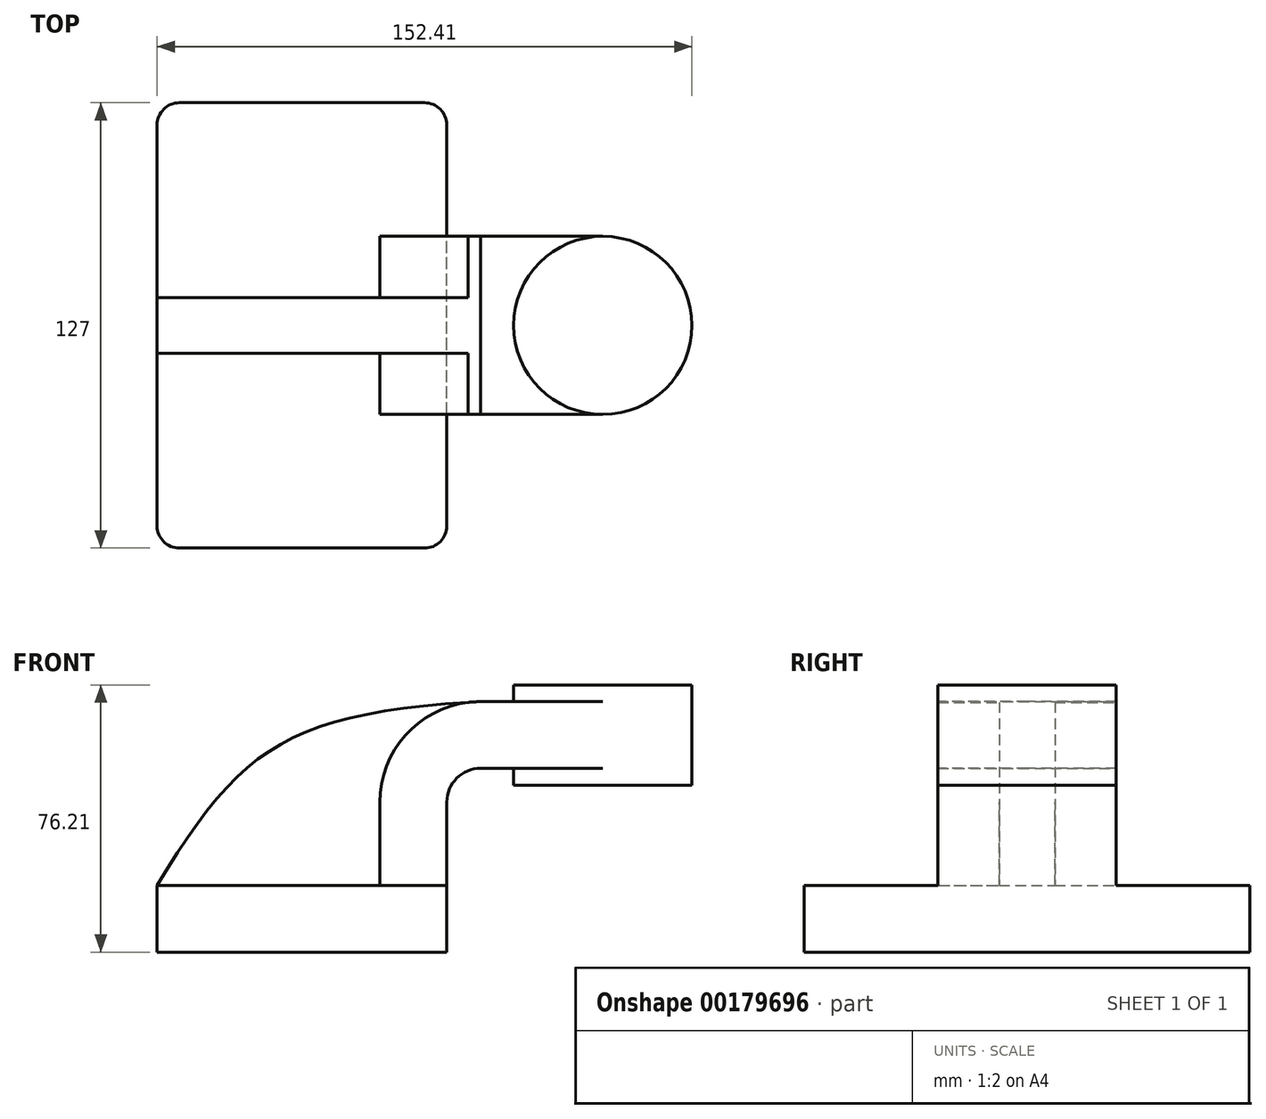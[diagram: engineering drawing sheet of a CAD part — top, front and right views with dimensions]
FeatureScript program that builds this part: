
annotation { "Feature Type Name" : "Feature", "Feature Type Description" : "" }
export const myFeature = defineFeature(function(context is Context, id is Id, definition is map)
    precondition{}
    {
        {
            var Q0;
            Q0=qCreatedBy(makeId("Front.planeOp"),FACE);
            var sketch = newSketch(context, id + "F0", { "sketchPlane" : qUnion([Q0])});
            skLineSegment(sketch, "E0.bottom", {"start": v(41.27, 9.53) * mm, "end": v(-41.28, 9.53) * mm});
            skLineSegment(sketch, "E0.top", {"start": v(41.28, -9.52) * mm, "end": v(-41.27, -9.52) * mm});
            skLineSegment(sketch, "E0.left", {"start": v(41.28, 9.53) * mm, "end": v(41.28, -9.52) * mm});
            skLineSegment(sketch, "E0.right", {"start": v(-41.28, 9.53) * mm, "end": v(-41.27, -9.52) * mm});
            skPoint(sketch, "E0.middle", {"position": v(0, 0) * mm});
            skLineSegment(sketch, "E1.bottom", {"start": v(111.12, 38.1) * mm, "end": v(60.32, 38.1) * mm});
            skLineSegment(sketch, "E1.top", {"start": v(111.12, 66.68) * mm, "end": v(60.32, 66.68) * mm});
            skLineSegment(sketch, "E1.left", {"start": v(111.12, 38.1) * mm, "end": v(111.12, 66.68) * mm});
            skLineSegment(sketch, "E1.right", {"start": v(60.32, 38.1) * mm, "end": v(60.32, 66.68) * mm});
            skPoint(sketch, "E1.middle", {"position": v(85.72, 52.39) * mm});
            skLineSegment(sketch, "E2", {"start": v(41.28, 9.53) * mm, "end": v(41.28, 33.25) * mm});
            skPoint(sketch, "E3.endSnap0", {"position": v(60.32, 52.39) * mm});
            skArc(sketch, "E4", {"start": v(41.27, 33.25) * mm, "mid": v(44.1, 40.06) * mm, "end": v(50.9, 42.88) * mm});
            skLineSegment(sketch, "E5", {"start": v(50.9, 42.88) * mm, "end": v(85.72, 42.88) * mm});
            skFitSpline(sketch, "E6", {"points": [v(50.9, 61.93) * mm, v(-41.28, 9.53) * mm], "startDerivative": vector(-164.5, -9.49) * mm, "endDerivative": vector(-71.06, -117.92) * mm});
            skLineSegment(sketch, "E7.0", {"start": v(50.9, 61.93) * mm, "end": v(85.72, 61.93) * mm});
            skArc(sketch, "E7.1", {"start": v(22.23, 33.25) * mm, "mid": v(30.62, 53.53) * mm, "end": v(50.9, 61.93) * mm});
            skLineSegment(sketch, "E7.2", {"start": v(22.23, 9.53) * mm, "end": v(22.23, 33.25) * mm});
            skLineSegment(sketch, "E8", {"start": v(85.72, 38.1) * mm, "end": v(85.72, 66.68) * mm});
            skSolve(sketch);
        }
        {
            var Q0;
            Q0=makeQuery(id+"F0.imprint","IMPRINT",FACE,{"disambiguationData":[TD([[makeQuery(id+"F0.imprint","IMPRINT",EDGE,{"derivedFrom":sQuery(id+"F0.wireOp",EDGE,"E0.top")}),-1.0]])]});
            extrude(context, id + "F1", {"entities" : qUnion([Q0]), "endBound" : BoundingType.SYMMETRIC, "depth" : 127 * mm});
        }
        {
            var Q0;
            {var subQ5=sQuery(id+"F0.wireOp",EDGE,"ryHTmhne-aWk1-Qow2-LsZY-GAX3mDUKrZVP");Q0=makeQuery(id+"F0.imprint","IMPRINT",FACE,{"disambiguationData":[TD([[makeQuery(id+"F0.imprint","IMPRINT",EDGE,{"derivedFrom":subQ5}),1.0]])]});}
            var Q1;
            {var subQ1=sQuery(id+"F0.wireOp",EDGE,"E2");Q1=makeQuery(id+"F0.imprint","IMPRINT",FACE,{"disambiguationData":[TD([[makeQuery(id+"F0.imprint","IMPRINT",EDGE,{"derivedFrom":subQ1}),1.0]])]});}
            var Q2;
            {var subQ0=sQuery(id+"F0.wireOp",EDGE,"E5");var subQ1=sQuery(id+"F0.wireOp",EDGE,"E1.right");var subQ2=makeQuery(id+"F0.imprint","INTERSECT",VERTEX,{"derivedFrom":[subQ1,subQ0]});Q2=makeQuery(id+"F0.imprint","IMPRINT",FACE,{"disambiguationData":[TD([[makeQuery(id+"F0.imprint","IMPRINT",EDGE,{"disambiguationData":[TD([[subQ2,-1.0]])],"derivedFrom":subQ1}),-1.0]])]});}
            extrude(context, id + "F2", {"entities" : qUnion([Q0, Q1, Q2]), "operationType" : NewBodyOperationType.ADD, "endBound" : BoundingType.SYMMETRIC, "depth" : 50.8 * mm});
        }
        {
            var Q0;
            {var subQ3=sQuery(id+"F0.wireOp",EDGE,"E7.2");Q0=makeQuery(id+"F0.imprint","IMPRINT",FACE,{"disambiguationData":[TD([[makeQuery(id+"F0.imprint","IMPRINT",EDGE,{"derivedFrom":subQ3}),1.0]])]});}
            extrude(context, id + "F3", {"entities" : qUnion([Q0]), "operationType" : NewBodyOperationType.ADD, "endBound" : BoundingType.SYMMETRIC, "depth" : 15.88 * mm});
        }
        {
            var Q0;
            {var subQ4=sQuery(id+"F0.wireOp",EDGE,"E1.left");Q0=makeQuery(id+"F0.imprint","IMPRINT",FACE,{"disambiguationData":[TD([[makeQuery(id+"F0.imprint","IMPRINT",EDGE,{"derivedFrom":subQ4}),1.0]])]});}
            var Q1;
            Q1=sQuery(id+"F0.wireOp",EDGE,"E8");
            revolve(context, id + "F4", {"operationType" : NewBodyOperationType.ADD, "entities" : qUnion([Q0]), "axis" : qUnion([Q1]), "revolveType" : RevolveType.FULL});
        }
        {
            var Q0;
            Q0=makeQuery(id+"F1.opExtrude","CAP_EDGE",EDGE,{"disambiguationData":[OSD([sQuery(id+"F0.wireOp",EDGE,"E0.left")])],"isStart":false});
            var Q1;
            Q1=makeQuery(id+"F1.opExtrude","CAP_EDGE",EDGE,{"disambiguationData":[OSD([sQuery(id+"F0.wireOp",EDGE,"E0.right")])],"isStart":false});
            var Q2;
            Q2=makeQuery(id+"F1.opExtrude","CAP_EDGE",EDGE,{"disambiguationData":[OSD([sQuery(id+"F0.wireOp",EDGE,"E0.left")])],"isStart":true});
            var Q3;
            Q3=makeQuery(id+"F1.opExtrude","CAP_EDGE",EDGE,{"disambiguationData":[OSD([sQuery(id+"F0.wireOp",EDGE,"E0.right")])],"isStart":true});
            fillet(context, id + "F5", {"entities" : qUnion([Q0, Q1, Q2, Q3]), "radius" : 6.35 * mm, "tangentPropagation" : true, "allowEdgeOverflow" : false});
        }
    });
